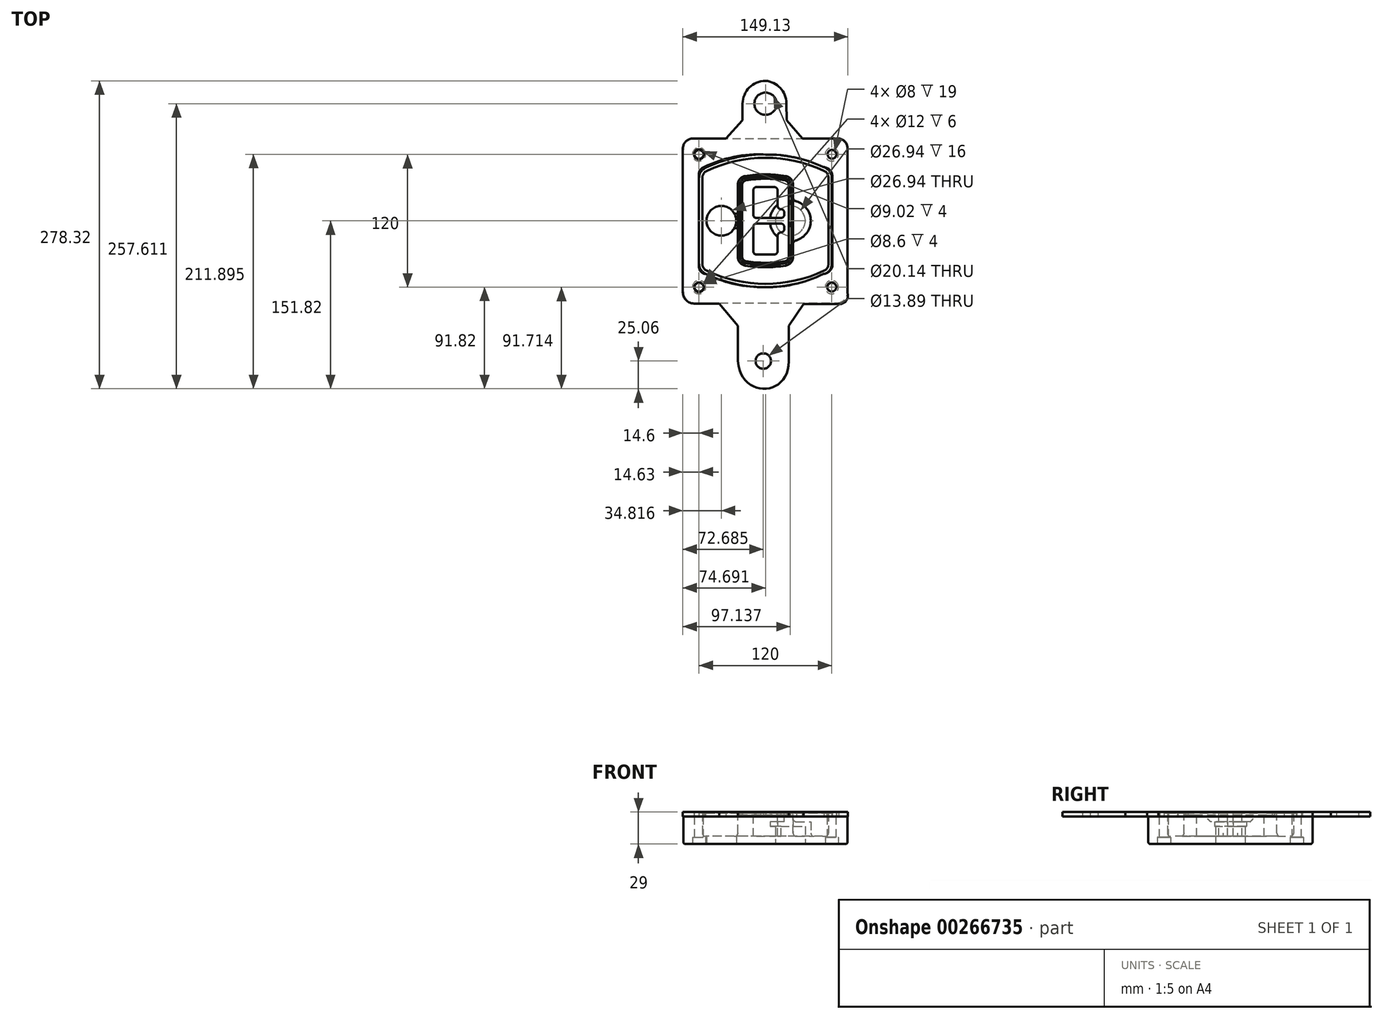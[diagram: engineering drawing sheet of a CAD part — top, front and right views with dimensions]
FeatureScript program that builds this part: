
annotation { "Feature Type Name" : "Feature", "Feature Type Description" : "" }
export const myFeature = defineFeature(function(context is Context, id is Id, definition is map)
    precondition{}
    {
        {
            var Q0;
            Q0=qCreatedBy(makeId("Top.planeOp"),FACE);
            var sketch = newSketch(context, id + "F0", { "sketchPlane" : qUnion([Q0])});
            skPoint(sketch, "E0.rect.middle", {"position": v(0, 0) * mm});
            skLineSegment(sketch, "E1.bottom", {"start": v(-64.25, -74.25) * mm, "end": v(64.25, -74.25) * mm});
            skLineSegment(sketch, "E1.top", {"start": v(-64.25, 74.25) * mm, "end": v(64.25, 74.25) * mm});
            skLineSegment(sketch, "E1.left", {"start": v(-74.25, -64.25) * mm, "end": v(-74.25, 64.25) * mm});
            skLineSegment(sketch, "E1.right", {"start": v(74.25, -64.25) * mm, "end": v(74.25, 64.25) * mm});
            skLineSegment(sketch, "E2", {"start": v(-74.25, 74.25) * mm, "end": v(74.25, -74.25) * mm, "construction": true});
            skLineSegment(sketch, "E3", {"start": v(74.25, 74.25) * mm, "end": v(-74.25, -74.25) * mm, "construction": true});
            skCircle(sketch, "E4", {"center": v(-60, 60) * mm, "radius": 4 * mm});
            skCircle(sketch, "E5", {"center": v(60, 60) * mm, "radius": 4 * mm});
            skCircle(sketch, "E6", {"center": v(60, -60) * mm, "radius": 4 * mm});
            skCircle(sketch, "E7", {"center": v(-60, -60) * mm, "radius": 4 * mm});
            skLineSegment(sketch, "E8", {"start": v(-60, 60) * mm, "end": v(60, 60) * mm, "construction": true});
            skLineSegment(sketch, "E9", {"start": v(60, 60) * mm, "end": v(60, -60) * mm, "construction": true});
            skLineSegment(sketch, "E10", {"start": v(60, -60) * mm, "end": v(-60, -60) * mm, "construction": true});
            skLineSegment(sketch, "E11", {"start": v(-60, -60) * mm, "end": v(-60, 60) * mm, "construction": true});
            skLineSegment(sketch, "E12", {"start": v(-60, 38.83) * mm, "end": v(-60, -38.83) * mm});
            skLineSegment(sketch, "E13", {"start": v(60, 38.83) * mm, "end": v(60, -38.83) * mm});
            skArc(sketch, "E14", {"start": v(54.26, 47.88) * mm, "mid": v(0, 60) * mm, "end": v(-54.26, 47.88) * mm});
            skArc(sketch, "E15", {"start": v(-54.26, -47.88) * mm, "mid": v(0, -60) * mm, "end": v(54.26, -47.88) * mm});
            skLineSegment(sketch, "E16", {"start": v(-60, 0) * mm, "end": v(60, 0) * mm, "construction": true});
            skPoint(sketch, "E17.visualSharp", {"position": v(-60, -45) * mm});
            skArc(sketch, "E17.filletArc", {"start": v(-60, -38.83) * mm, "mid": v(-58.44, -44.2) * mm, "end": v(-54.26, -47.88) * mm});
            skPoint(sketch, "E18.visualSharp", {"position": v(-60, 45) * mm});
            skArc(sketch, "E18.filletArc", {"start": v(-54.26, 47.88) * mm, "mid": v(-58.44, 44.2) * mm, "end": v(-60, 38.83) * mm});
            skPoint(sketch, "E19.visualSharp", {"position": v(60, 45) * mm});
            skArc(sketch, "E19.filletArc", {"start": v(60, 38.83) * mm, "mid": v(58.44, 44.2) * mm, "end": v(54.26, 47.88) * mm});
            skPoint(sketch, "E20.visualSharp", {"position": v(60, -45) * mm});
            skArc(sketch, "E20.filletArc", {"start": v(54.26, -47.88) * mm, "mid": v(58.44, -44.2) * mm, "end": v(60, -38.83) * mm});
            skPoint(sketch, "E21.visualSharp", {"position": v(-74.25, 74.25) * mm});
            skArc(sketch, "E21.filletArc", {"start": v(-64.25, 74.25) * mm, "mid": v(-71.32, 71.32) * mm, "end": v(-74.25, 64.25) * mm});
            skPoint(sketch, "E22.visualSharp", {"position": v(74.25, 74.25) * mm});
            skArc(sketch, "E22.filletArc", {"start": v(74.25, 64.25) * mm, "mid": v(71.32, 71.32) * mm, "end": v(64.25, 74.25) * mm});
            skPoint(sketch, "E23.visualSharp", {"position": v(74.25, -74.25) * mm});
            skArc(sketch, "E23.filletArc", {"start": v(64.25, -74.25) * mm, "mid": v(71.32, -71.32) * mm, "end": v(74.25, -64.25) * mm});
            skPoint(sketch, "E24.visualSharp", {"position": v(-74.25, -74.25) * mm});
            skArc(sketch, "E24.filletArc", {"start": v(-74.25, -64.25) * mm, "mid": v(-71.32, -71.32) * mm, "end": v(-64.25, -74.25) * mm});
            skArc(sketch, "E25.0", {"start": v(57, 38.83) * mm, "mid": v(55.9, 42.58) * mm, "end": v(52.98, 45.17) * mm});
            skLineSegment(sketch, "E25.1", {"start": v(57, 38.83) * mm, "end": v(57, -38.83) * mm});
            skArc(sketch, "E25.2", {"start": v(52.98, -45.17) * mm, "mid": v(55.9, -42.58) * mm, "end": v(57, -38.83) * mm});
            skArc(sketch, "E25.3", {"start": v(-52.98, -45.17) * mm, "mid": v(0, -57) * mm, "end": v(52.98, -45.17) * mm});
            skArc(sketch, "E25.4", {"start": v(-57, -38.83) * mm, "mid": v(-55.9, -42.58) * mm, "end": v(-52.98, -45.17) * mm});
            skArc(sketch, "E25.5", {"start": v(52.98, 45.17) * mm, "mid": v(0, 57) * mm, "end": v(-52.98, 45.17) * mm});
            skLineSegment(sketch, "E25.6", {"start": v(-57, 38.83) * mm, "end": v(-57, -38.83) * mm});
            skArc(sketch, "E25.7", {"start": v(-52.98, 45.17) * mm, "mid": v(-55.9, 42.58) * mm, "end": v(-57, 38.83) * mm});
            skArc(sketch, "E26.0", {"start": v(-55.96, 51.5) * mm, "mid": v(-61.82, 46.33) * mm, "end": v(-64, 38.83) * mm});
            skArc(sketch, "E26.1", {"start": v(55.96, 51.5) * mm, "mid": v(0, 64) * mm, "end": v(-55.96, 51.5) * mm});
            skArc(sketch, "E26.2", {"start": v(64, 38.83) * mm, "mid": v(61.82, 46.33) * mm, "end": v(55.96, 51.5) * mm});
            skLineSegment(sketch, "E26.3", {"start": v(64, 38.83) * mm, "end": v(64, -38.83) * mm});
            skArc(sketch, "E26.4", {"start": v(55.96, -51.5) * mm, "mid": v(61.82, -46.33) * mm, "end": v(64, -38.83) * mm});
            skLineSegment(sketch, "E26.5", {"start": v(-64, 38.83) * mm, "end": v(-64, -38.83) * mm});
            skArc(sketch, "E26.6", {"start": v(-55.96, -51.5) * mm, "mid": v(0, -64) * mm, "end": v(55.96, -51.5) * mm});
            skArc(sketch, "E26.7", {"start": v(-64, -38.83) * mm, "mid": v(-61.82, -46.33) * mm, "end": v(-55.96, -51.5) * mm});
            skSolve(sketch);
        }
        {
            var Q0;
            Q0=makeQuery(id+"F0.imprint","IMPRINT",FACE,{"disambiguationData":[TD([[makeQuery(id+"F0.imprint","IMPRINT",EDGE,{"derivedFrom":sQuery(id+"F0.wireOp",EDGE,"E1.bottom")}),1.0]])]});
            var Q1;
            Q1=makeQuery(id+"F0.imprint","IMPRINT",FACE,{"disambiguationData":[TD([[makeQuery(id+"F0.imprint","IMPRINT",EDGE,{"derivedFrom":sQuery(id+"F0.wireOp",EDGE,"E12")}),1.0]])]});
            var Q2;
            Q2=makeQuery(id+"F0.imprint","IMPRINT",FACE,{"disambiguationData":[TD([[makeQuery(id+"F0.imprint","IMPRINT",EDGE,{"derivedFrom":sQuery(id+"F0.wireOp",EDGE,"E25.0")}),1.0]])]});
            var Q3;
            Q3=makeQuery(id+"F0.imprint","IMPRINT",FACE,{"disambiguationData":[TD([[makeQuery(id+"F0.imprint","IMPRINT",EDGE,{"derivedFrom":sQuery(id+"F0.wireOp",EDGE,"E12")}),-1.0]])]});
            extrude(context, id + "F1", {"entities" : qUnion([Q0, Q1, Q2, Q3]), "oppositeDirection" : true, "depth" : 25 * mm});
        }
        {
            var Q0;
            Q0=makeQuery(id+"F0.imprint","IMPRINT",FACE,{"disambiguationData":[TD([[makeQuery(id+"F0.imprint","IMPRINT",EDGE,{"derivedFrom":sQuery(id+"F0.wireOp",EDGE,"E12")}),1.0]])]});
            extrude(context, id + "F2", {"entities" : qUnion([Q0]), "operationType" : NewBodyOperationType.ADD, "depth" : 3 * mm});
        }
        {
            var Q0;
            Q0=makeQuery(id+"F0.imprint","IMPRINT",FACE,{"disambiguationData":[TD([[makeQuery(id+"F0.imprint","IMPRINT",EDGE,{"derivedFrom":sQuery(id+"F0.wireOp",EDGE,"E25.0")}),1.0]])]});
            extrude(context, id + "F3", {"entities" : qUnion([Q0]), "operationType" : NewBodyOperationType.REMOVE, "oppositeDirection" : true, "depth" : 18 * mm});
        }
        {
            var Q0;
            Q0=makeQuery(id+"F2.opExtrude","CAP_FACE",FACE,{"disambiguationData":[OSD([sQuery(id+"F0.wireOp",EDGE,"E12"),sQuery(id+"F0.wireOp",EDGE,"E13"),sQuery(id+"F0.wireOp",EDGE,"E14"),sQuery(id+"F0.wireOp",EDGE,"E15"),sQuery(id+"F0.wireOp",EDGE,"E17.filletArc"),sQuery(id+"F0.wireOp",EDGE,"E18.filletArc"),sQuery(id+"F0.wireOp",EDGE,"E19.filletArc"),sQuery(id+"F0.wireOp",EDGE,"E20.filletArc"),sQuery(id+"F0.wireOp",EDGE,"E25.0"),sQuery(id+"F0.wireOp",EDGE,"E25.1"),sQuery(id+"F0.wireOp",EDGE,"E25.2"),sQuery(id+"F0.wireOp",EDGE,"E25.3"),sQuery(id+"F0.wireOp",EDGE,"E25.4"),sQuery(id+"F0.wireOp",EDGE,"E25.5"),sQuery(id+"F0.wireOp",EDGE,"E25.6"),sQuery(id+"F0.wireOp",EDGE,"E25.7")])],"isStart":false});
            var sketch = newSketch(context, id + "F4", { "sketchPlane" : qUnion([Q0])});
            skArc(sketch, "E27.0", {"start": v(-18.34, -40.45) * mm, "mid": v(0, -42) * mm, "end": v(18.34, -40.45) * mm});
            skArc(sketch, "E28.0", {"start": v(18.34, 40.45) * mm, "mid": v(0, 42) * mm, "end": v(-18.34, 40.45) * mm});
            skLineSegment(sketch, "E29", {"start": v(-25, 32.57) * mm, "end": v(-25, -32.57) * mm});
            skLineSegment(sketch, "E30", {"start": v(25, 32.57) * mm, "end": v(25, -32.57) * mm});
            skLineSegment(sketch, "E31", {"start": v(-25, 39.1) * mm, "end": v(25, 39.1) * mm, "construction": true});
            skLineSegment(sketch, "E32", {"start": v(-25, -39.1) * mm, "end": v(25, -39.1) * mm, "construction": true});
            skPoint(sketch, "E33.visualSharp", {"position": v(-25, 39.1) * mm});
            skArc(sketch, "E33.filletArc", {"start": v(-18.34, 40.45) * mm, "mid": v(-23.11, 37.73) * mm, "end": v(-25, 32.57) * mm});
            skPoint(sketch, "E34.visualSharp", {"position": v(25, 39.1) * mm});
            skArc(sketch, "E34.filletArc", {"start": v(25, 32.57) * mm, "mid": v(23.11, 37.73) * mm, "end": v(18.34, 40.45) * mm});
            skPoint(sketch, "E35.visualSharp", {"position": v(25, -39.1) * mm});
            skArc(sketch, "E35.filletArc", {"start": v(18.34, -40.45) * mm, "mid": v(23.11, -37.73) * mm, "end": v(25, -32.57) * mm});
            skPoint(sketch, "E36.visualSharp", {"position": v(-25, -39.1) * mm});
            skArc(sketch, "E36.filletArc", {"start": v(-25, -32.57) * mm, "mid": v(-23.11, -37.73) * mm, "end": v(-18.34, -40.45) * mm});
            skArc(sketch, "E37.0", {"start": v(52.98, 45.17) * mm, "mid": v(0, 57) * mm, "end": v(-52.98, 45.17) * mm});
            skArc(sketch, "E37.1", {"start": v(-52.98, 45.17) * mm, "mid": v(-55.9, 42.58) * mm, "end": v(-57, 38.83) * mm});
            skLineSegment(sketch, "E37.2", {"start": v(-57, 38.83) * mm, "end": v(-57, -38.83) * mm});
            skArc(sketch, "E37.3", {"start": v(-57, -38.83) * mm, "mid": v(-55.9, -42.58) * mm, "end": v(-52.98, -45.17) * mm});
            skArc(sketch, "E37.4", {"start": v(-52.98, -45.17) * mm, "mid": v(0, -57) * mm, "end": v(52.98, -45.17) * mm});
            skArc(sketch, "E37.5", {"start": v(52.98, -45.17) * mm, "mid": v(55.9, -42.58) * mm, "end": v(57, -38.83) * mm});
            skLineSegment(sketch, "E37.6", {"start": v(57, 38.83) * mm, "end": v(57, -38.83) * mm});
            skArc(sketch, "E37.7", {"start": v(57, 38.83) * mm, "mid": v(55.9, 42.58) * mm, "end": v(52.98, 45.17) * mm});
            skLineSegment(sketch, "E38.0", {"start": v(23, 32.57) * mm, "end": v(23, -32.57) * mm});
            skArc(sketch, "E38.1", {"start": v(18, -38.48) * mm, "mid": v(21.58, -36.44) * mm, "end": v(23, -32.57) * mm});
            skArc(sketch, "E38.2", {"start": v(-18, -38.48) * mm, "mid": v(0, -40) * mm, "end": v(18, -38.48) * mm});
            skArc(sketch, "E38.3", {"start": v(-23, -32.57) * mm, "mid": v(-21.58, -36.44) * mm, "end": v(-18, -38.48) * mm});
            skLineSegment(sketch, "E38.4", {"start": v(-23, 32.57) * mm, "end": v(-23, -32.57) * mm});
            skArc(sketch, "E38.5", {"start": v(23, 32.57) * mm, "mid": v(21.58, 36.44) * mm, "end": v(18, 38.48) * mm});
            skArc(sketch, "E38.6", {"start": v(-18, 38.48) * mm, "mid": v(-21.58, 36.44) * mm, "end": v(-23, 32.57) * mm});
            skArc(sketch, "E38.7", {"start": v(18, 38.48) * mm, "mid": v(0, 40) * mm, "end": v(-18, 38.48) * mm});
            skArc(sketch, "E39.0", {"start": v(21, 32.57) * mm, "mid": v(20.06, 35.15) * mm, "end": v(17.67, 36.5) * mm});
            skLineSegment(sketch, "E39.1", {"start": v(21, 32.57) * mm, "end": v(21, -32.57) * mm});
            skArc(sketch, "E39.2", {"start": v(17.67, -36.5) * mm, "mid": v(20.06, -35.15) * mm, "end": v(21, -32.57) * mm});
            skArc(sketch, "E39.3", {"start": v(-17.67, -36.5) * mm, "mid": v(0, -38) * mm, "end": v(17.67, -36.5) * mm});
            skArc(sketch, "E39.4", {"start": v(-21, -32.57) * mm, "mid": v(-20.06, -35.15) * mm, "end": v(-17.67, -36.5) * mm});
            skArc(sketch, "E39.5", {"start": v(17.67, 36.5) * mm, "mid": v(0, 38) * mm, "end": v(-17.67, 36.5) * mm});
            skLineSegment(sketch, "E39.6", {"start": v(-21, 32.57) * mm, "end": v(-21, -32.57) * mm});
            skArc(sketch, "E39.7", {"start": v(-17.67, 36.5) * mm, "mid": v(-20.06, 35.15) * mm, "end": v(-21, 32.57) * mm});
            skLineSegment(sketch, "E40", {"start": v(-25, 0) * mm, "end": v(25, 0) * mm, "construction": true});
            skLineSegment(sketch, "E41", {"start": v(-11, 5.5) * mm, "end": v(-11, 27.5) * mm});
            skLineSegment(sketch, "E42", {"start": v(-8, 30.5) * mm, "end": v(8, 30.5) * mm});
            skLineSegment(sketch, "E43", {"start": v(11, 27.5) * mm, "end": v(11, 13.5) * mm});
            skLineSegment(sketch, "E44", {"start": v(14, 10.5) * mm, "end": v(14, 10.5) * mm});
            skLineSegment(sketch, "E45", {"start": v(17, 7.5) * mm, "end": v(17, 5.5) * mm});
            skLineSegment(sketch, "E46", {"start": v(14, 2.5) * mm, "end": v(-8, 2.5) * mm});
            skPoint(sketch, "E47.visualSharp", {"position": v(-11, 30.5) * mm});
            skArc(sketch, "E47.filletArc", {"start": v(-8, 30.5) * mm, "mid": v(-10.12, 29.62) * mm, "end": v(-11, 27.5) * mm});
            skPoint(sketch, "E48.visualSharp", {"position": v(11, 30.5) * mm});
            skArc(sketch, "E48.filletArc", {"start": v(11, 27.5) * mm, "mid": v(10.12, 29.62) * mm, "end": v(8, 30.5) * mm});
            skPoint(sketch, "E49.visualSharp", {"position": v(11, 10.5) * mm});
            skArc(sketch, "E49.filletArc", {"start": v(11, 13.5) * mm, "mid": v(11.88, 11.38) * mm, "end": v(14, 10.5) * mm});
            skPoint(sketch, "E50.visualSharp", {"position": v(17, 10.5) * mm});
            skArc(sketch, "E50.filletArc", {"start": v(17, 7.5) * mm, "mid": v(16.12, 9.62) * mm, "end": v(14, 10.5) * mm});
            skPoint(sketch, "E51.visualSharp", {"position": v(17, 2.5) * mm});
            skArc(sketch, "E51.filletArc", {"start": v(14, 2.5) * mm, "mid": v(16.12, 3.38) * mm, "end": v(17, 5.5) * mm});
            skPoint(sketch, "E52.visualSharp", {"position": v(-11, 2.5) * mm});
            skArc(sketch, "E52.filletArc", {"start": v(-11, 5.5) * mm, "mid": v(-10.12, 3.38) * mm, "end": v(-8, 2.5) * mm});
            skLineSegment(sketch, "E53.0.MirrorCS", {"start": v(14, -2.5) * mm, "end": v(-8, -2.5) * mm});
            skArc(sketch, "E54.0.MirrorCS", {"start": v(-11, -5.5) * mm, "mid": v(-10.12, -3.38) * mm, "end": v(-8, -2.5) * mm});
            skLineSegment(sketch, "E55.0.MirrorCS", {"start": v(-11, -5.5) * mm, "end": v(-11, -27.5) * mm});
            skArc(sketch, "E56.0.MirrorCS", {"start": v(-8, -30.5) * mm, "mid": v(-10.12, -29.62) * mm, "end": v(-11, -27.5) * mm});
            skLineSegment(sketch, "E57.0.MirrorCS", {"start": v(-8, -30.5) * mm, "end": v(8, -30.5) * mm});
            skArc(sketch, "E58.0.MirrorCS", {"start": v(11, -27.5) * mm, "mid": v(10.12, -29.62) * mm, "end": v(8, -30.5) * mm});
            skLineSegment(sketch, "E59.0.MirrorCS", {"start": v(11, -27.5) * mm, "end": v(11, -13.5) * mm});
            skArc(sketch, "E60.0.MirrorCS", {"start": v(11, -13.5) * mm, "mid": v(11.88, -11.38) * mm, "end": v(14, -10.5) * mm});
            skArc(sketch, "E61.0.MirrorCS", {"start": v(17, -7.5) * mm, "mid": v(16.12, -9.62) * mm, "end": v(14, -10.5) * mm});
            skLineSegment(sketch, "E62.0.MirrorCS", {"start": v(17, -7.5) * mm, "end": v(17, -5.5) * mm});
            skArc(sketch, "E63.0.MirrorCS", {"start": v(14, -2.5) * mm, "mid": v(16.12, -3.38) * mm, "end": v(17, -5.5) * mm});
            skSolve(sketch);
        }
        {
            var Q0;
            Q0=makeQuery(id+"F4.imprint","IMPRINT",FACE,{"disambiguationData":[TD([[makeQuery(id+"F4.imprint","IMPRINT",EDGE,{"derivedFrom":sQuery(id+"F4.wireOp",EDGE,"E27.0")}),1.0]])]});
            var Q1;
            Q1=makeQuery(id+"F4.imprint","IMPRINT",FACE,{"disambiguationData":[TD([[makeQuery(id+"F4.imprint","IMPRINT",EDGE,{"derivedFrom":sQuery(id+"F4.wireOp",EDGE,"E38.0")}),-1.0]])]});
            var Q2;
            Q2=makeQuery(id+"F4.imprint","IMPRINT",FACE,{"disambiguationData":[TD([[makeQuery(id+"F4.imprint","IMPRINT",EDGE,{"derivedFrom":sQuery(id+"F4.wireOp",EDGE,"E39.0")}),1.0]])]});
            extrude(context, id + "F5", {"entities" : qUnion([Q0, Q1, Q2]), "operationType" : NewBodyOperationType.ADD, "endBound" : BoundingType.UP_TO_NEXT, "oppositeDirection" : true, "depth" : 25 * mm});
        }
        {
            var Q0;
            Q0=makeQuery(id+"F4.imprint","IMPRINT",FACE,{"disambiguationData":[TD([[makeQuery(id+"F4.imprint","IMPRINT",EDGE,{"derivedFrom":sQuery(id+"F4.wireOp",EDGE,"E38.0")}),-1.0]])]});
            extrude(context, id + "F6", {"entities" : qUnion([Q0]), "operationType" : NewBodyOperationType.REMOVE, "oppositeDirection" : true, "depth" : 2 * mm});
        }
        {
            var Q0;
            Q0=makeQuery(id+"F1.opExtrude","CAP_FACE",FACE,{"disambiguationData":[OSD([sQuery(id+"F0.wireOp",EDGE,"E1.bottom"),sQuery(id+"F0.wireOp",EDGE,"E1.top"),sQuery(id+"F0.wireOp",EDGE,"E1.left"),sQuery(id+"F0.wireOp",EDGE,"E1.right"),sQuery(id+"F0.wireOp",EDGE,"E4"),sQuery(id+"F0.wireOp",EDGE,"E5"),sQuery(id+"F0.wireOp",EDGE,"E6"),sQuery(id+"F0.wireOp",EDGE,"E7"),sQuery(id+"F0.wireOp",EDGE,"E21.filletArc"),sQuery(id+"F0.wireOp",EDGE,"E22.filletArc"),sQuery(id+"F0.wireOp",EDGE,"E23.filletArc"),sQuery(id+"F0.wireOp",EDGE,"E24.filletArc")])],"isStart":false});
            var sketch = newSketch(context, id + "F7", { "sketchPlane" : qUnion([Q0])});
            skCircle(sketch, "E64", {"center": v(22.5, 0) * mm, "radius": 13.47 * mm});
            skCircle(sketch, "E65", {"center": v(-39.81, 0) * mm, "radius": 13.47 * mm});
            skLineSegment(sketch, "E66", {"start": v(74.25, 0) * mm, "end": v(-74.25, 0) * mm});
            skCircle(sketch, "E67", {"center": v(22.5, 0) * mm, "radius": 18.47 * mm});
            skCircle(sketch, "E68", {"center": v(60, -60) * mm, "radius": 6 * mm});
            skCircle(sketch, "E69", {"center": v(-60, -60) * mm, "radius": 6 * mm});
            skCircle(sketch, "E70", {"center": v(-60, 60) * mm, "radius": 6 * mm});
            skCircle(sketch, "E71", {"center": v(60, 60) * mm, "radius": 6 * mm});
            skSolve(sketch);
        }
        {
            var Q0;
            {var subQ1=sQuery(id+"F7.wireOp",EDGE,"E66");var subQ4=sQuery(id+"F7.wireOp",EDGE,"E64");var subQ6=makeQuery(id+"F7.imprint","INTERSECT",VERTEX,{"disambiguationData":[OD(0.0)],"derivedFrom":[subQ4,subQ1]});Q0=makeQuery(id+"F7.imprint","IMPRINT",FACE,{"disambiguationData":[TD([[makeQuery(id+"F7.imprint","IMPRINT",EDGE,{"disambiguationData":[TD([[subQ6,-1.0]])],"derivedFrom":subQ4}),-1.0]])]});}
            var Q1;
            {var subQ0=sQuery(id+"F7.wireOp",EDGE,"E66");var subQ1=sQuery(id+"F7.wireOp",EDGE,"E64");var subQ3=makeQuery(id+"F7.imprint","INTERSECT",VERTEX,{"disambiguationData":[OD(0.0)],"derivedFrom":[subQ1,subQ0]});Q1=makeQuery(id+"F7.imprint","IMPRINT",FACE,{"disambiguationData":[TD([[makeQuery(id+"F7.imprint","IMPRINT",EDGE,{"disambiguationData":[TD([[subQ3,-1.0]])],"derivedFrom":subQ1}),1.0]])]});}
            var Q2;
            {var subQ0=sQuery(id+"F7.wireOp",EDGE,"E66");var subQ1=sQuery(id+"F7.wireOp",EDGE,"E64");var subQ3=makeQuery(id+"F7.imprint","INTERSECT",VERTEX,{"disambiguationData":[OD(0.0)],"derivedFrom":[subQ1,subQ0]});Q2=makeQuery(id+"F7.imprint","IMPRINT",FACE,{"disambiguationData":[TD([[makeQuery(id+"F7.imprint","IMPRINT",EDGE,{"disambiguationData":[TD([[subQ3,1.0]])],"derivedFrom":subQ1}),1.0]])]});}
            var Q3;
            {var subQ1=sQuery(id+"F7.wireOp",EDGE,"E66");var subQ4=sQuery(id+"F7.wireOp",EDGE,"E64");var subQ6=makeQuery(id+"F7.imprint","INTERSECT",VERTEX,{"disambiguationData":[OD(0.0)],"derivedFrom":[subQ4,subQ1]});Q3=makeQuery(id+"F7.imprint","IMPRINT",FACE,{"disambiguationData":[TD([[makeQuery(id+"F7.imprint","IMPRINT",EDGE,{"disambiguationData":[TD([[subQ6,1.0]])],"derivedFrom":subQ4}),-1.0]])]});}
            extrude(context, id + "F8", {"entities" : qUnion([Q0, Q1, Q2, Q3]), "operationType" : NewBodyOperationType.ADD, "oppositeDirection" : true, "depth" : 20 * mm});
        }
        {
            var Q0;
            {var subQ0=sQuery(id+"F7.wireOp",EDGE,"E66");var subQ1=sQuery(id+"F7.wireOp",EDGE,"E64");var subQ3=makeQuery(id+"F7.imprint","INTERSECT",VERTEX,{"disambiguationData":[OD(0.0)],"derivedFrom":[subQ1,subQ0]});Q0=makeQuery(id+"F7.imprint","IMPRINT",FACE,{"disambiguationData":[TD([[makeQuery(id+"F7.imprint","IMPRINT",EDGE,{"disambiguationData":[TD([[subQ3,-1.0]])],"derivedFrom":subQ1}),1.0]])]});}
            var Q1;
            {var subQ0=sQuery(id+"F7.wireOp",EDGE,"E66");var subQ1=sQuery(id+"F7.wireOp",EDGE,"E64");var subQ3=makeQuery(id+"F7.imprint","INTERSECT",VERTEX,{"disambiguationData":[OD(0.0)],"derivedFrom":[subQ1,subQ0]});Q1=makeQuery(id+"F7.imprint","IMPRINT",FACE,{"disambiguationData":[TD([[makeQuery(id+"F7.imprint","IMPRINT",EDGE,{"disambiguationData":[TD([[subQ3,1.0]])],"derivedFrom":subQ1}),1.0]])]});}
            extrude(context, id + "F9", {"entities" : qUnion([Q0, Q1]), "operationType" : NewBodyOperationType.REMOVE, "oppositeDirection" : true, "depth" : 16 * mm});
        }
        {
            var Q0;
            {var subQ0=sQuery(id+"F7.wireOp",EDGE,"E66");var subQ1=sQuery(id+"F7.wireOp",EDGE,"E65");var subQ3=makeQuery(id+"F7.imprint","INTERSECT",VERTEX,{"disambiguationData":[OD(0.0)],"derivedFrom":[subQ1,subQ0]});Q0=makeQuery(id+"F7.imprint","IMPRINT",FACE,{"disambiguationData":[TD([[makeQuery(id+"F7.imprint","IMPRINT",EDGE,{"disambiguationData":[TD([[subQ3,-1.0]])],"derivedFrom":subQ1}),1.0]])]});}
            var Q1;
            {var subQ0=sQuery(id+"F7.wireOp",EDGE,"E66");var subQ1=sQuery(id+"F7.wireOp",EDGE,"E65");var subQ3=makeQuery(id+"F7.imprint","INTERSECT",VERTEX,{"disambiguationData":[OD(0.0)],"derivedFrom":[subQ1,subQ0]});Q1=makeQuery(id+"F7.imprint","IMPRINT",FACE,{"disambiguationData":[TD([[makeQuery(id+"F7.imprint","IMPRINT",EDGE,{"disambiguationData":[TD([[subQ3,1.0]])],"derivedFrom":subQ1}),1.0]])]});}
            extrude(context, id + "F10", {"entities" : qUnion([Q0, Q1]), "operationType" : NewBodyOperationType.REMOVE, "oppositeDirection" : true, "depth" : 25 * mm});
        }
        {
            var Q0;
            Q0=makeQuery(id+"F7.imprint","IMPRINT",FACE,{"disambiguationData":[TD([[makeQuery(id+"F7.imprint","IMPRINT",EDGE,{"derivedFrom":sQuery(id+"F7.wireOp",EDGE,"E68")}),1.0]])]});
            var Q1;
            Q1=makeQuery(id+"F7.imprint","IMPRINT",FACE,{"disambiguationData":[TD([[makeQuery(id+"F7.imprint","IMPRINT",EDGE,{"derivedFrom":makeQuery(id+"F1.opExtrude","CAP_EDGE",EDGE,{"disambiguationData":[OSD([sQuery(id+"F0.wireOp",EDGE,"E5")])],"isStart":false})}),-1.0]])]});
            var Q2;
            Q2=makeQuery(id+"F7.imprint","IMPRINT",FACE,{"disambiguationData":[TD([[makeQuery(id+"F7.imprint","IMPRINT",EDGE,{"derivedFrom":sQuery(id+"F7.wireOp",EDGE,"E69")}),1.0]])]});
            var Q3;
            Q3=makeQuery(id+"F7.imprint","IMPRINT",FACE,{"disambiguationData":[TD([[makeQuery(id+"F7.imprint","IMPRINT",EDGE,{"derivedFrom":makeQuery(id+"F1.opExtrude","CAP_EDGE",EDGE,{"disambiguationData":[OSD([sQuery(id+"F0.wireOp",EDGE,"E4")])],"isStart":false})}),-1.0]])]});
            var Q4;
            Q4=makeQuery(id+"F7.imprint","IMPRINT",FACE,{"disambiguationData":[TD([[makeQuery(id+"F7.imprint","IMPRINT",EDGE,{"derivedFrom":sQuery(id+"F7.wireOp",EDGE,"E70")}),1.0]])]});
            var Q5;
            Q5=makeQuery(id+"F7.imprint","IMPRINT",FACE,{"disambiguationData":[TD([[makeQuery(id+"F7.imprint","IMPRINT",EDGE,{"derivedFrom":makeQuery(id+"F1.opExtrude","CAP_EDGE",EDGE,{"disambiguationData":[OSD([sQuery(id+"F0.wireOp",EDGE,"E7")])],"isStart":false})}),-1.0]])]});
            var Q6;
            Q6=makeQuery(id+"F7.imprint","IMPRINT",FACE,{"disambiguationData":[TD([[makeQuery(id+"F7.imprint","IMPRINT",EDGE,{"derivedFrom":sQuery(id+"F7.wireOp",EDGE,"E71")}),1.0]])]});
            var Q7;
            Q7=makeQuery(id+"F7.imprint","IMPRINT",FACE,{"disambiguationData":[TD([[makeQuery(id+"F7.imprint","IMPRINT",EDGE,{"derivedFrom":makeQuery(id+"F1.opExtrude","CAP_EDGE",EDGE,{"disambiguationData":[OSD([sQuery(id+"F0.wireOp",EDGE,"E6")])],"isStart":false})}),-1.0]])]});
            extrude(context, id + "F11", {"entities" : qUnion([Q0, Q1, Q2, Q3, Q4, Q5, Q6, Q7]), "operationType" : NewBodyOperationType.REMOVE, "oppositeDirection" : true, "depth" : 6 * mm});
        }
        {
            var Q0;
            Q0=makeQuery(id+"F9.boolean.opBoolean","COPY",FACE,{"derivedFrom":makeQuery(id+"F9.opExtrude","CAP_FACE",FACE,{"disambiguationData":[OSD([sQuery(id+"F7.wireOp",EDGE,"E64")])],"isStart":false})});
            var sketch = newSketch(context, id + "F12", { "sketchPlane" : qUnion([Q0])});
            skArc(sketch, "E72.0", {"start": v(11, 14.45) * mm, "mid": v(6.45, 9.13) * mm, "end": v(4.2, 2.5) * mm});
            skArc(sketch, "E72.1", {"start": v(4.2, -2.5) * mm, "mid": v(6.45, -9.13) * mm, "end": v(11, -14.45) * mm});
            skLineSegment(sketch, "E73", {"start": v(4.2, -2.5) * mm, "end": v(14, -2.5) * mm});
            skLineSegment(sketch, "E74.0", {"start": v(14, 2.5) * mm, "end": v(4.2, 2.5) * mm});
            skArc(sketch, "E74.1", {"start": v(14, 2.5) * mm, "mid": v(16.12, 3.38) * mm, "end": v(17, 5.5) * mm});
            skLineSegment(sketch, "E74.2", {"start": v(17, 7.5) * mm, "end": v(17, 5.5) * mm});
            skArc(sketch, "E74.3", {"start": v(17, 7.5) * mm, "mid": v(16.12, 9.62) * mm, "end": v(14, 10.5) * mm});
            skArc(sketch, "E74.4", {"start": v(11, 13.5) * mm, "mid": v(11.88, 11.38) * mm, "end": v(14, 10.5) * mm});
            skLineSegment(sketch, "E74.5", {"start": v(11, 14.45) * mm, "end": v(11, 13.5) * mm});
            skLineSegment(sketch, "E74.7", {"start": v(14, -2.5) * mm, "end": v(4.2, -2.5) * mm});
            skArc(sketch, "E74.8", {"start": v(14, -2.5) * mm, "mid": v(16.12, -3.38) * mm, "end": v(17, -5.5) * mm});
            skLineSegment(sketch, "E74.9", {"start": v(17, -7.5) * mm, "end": v(17, -5.5) * mm});
            skArc(sketch, "E74.10", {"start": v(17, -7.5) * mm, "mid": v(16.12, -9.62) * mm, "end": v(14, -10.5) * mm});
            skArc(sketch, "E74.11", {"start": v(11, -13.5) * mm, "mid": v(11.88, -11.38) * mm, "end": v(14, -10.5) * mm});
            skLineSegment(sketch, "E74.12", {"start": v(11, -14.45) * mm, "end": v(11, -13.5) * mm});
            skPoint(sketch, "E75.orphan", {"position": v(11, -27.5) * mm});
            skPoint(sketch, "E76.orphan", {"position": v(-8, -2.5) * mm});
            skPoint(sketch, "E77.orphan", {"position": v(-8, 2.5) * mm});
            skPoint(sketch, "E78.orphan", {"position": v(11, 27.5) * mm});
            skSolve(sketch);
        }
        {
            var Q0;
            {var subQ7=sQuery(id+"F12.wireOp",EDGE,"E72.0");var subQ14=sQuery(id+"F12.wireOp",EDGE,"E72.1");var subQ16=sQuery(id+"F12.wireOp",EDGE,"E74.1");var subQ18=sQuery(id+"F12.wireOp",EDGE,"E74.8");Q0=qUnion([makeQuery(id+"F12.imprint","IMPRINT",FACE,{"disambiguationData":[TD([[makeQuery(id+"F12.imprint","IMPRINT",EDGE,{"derivedFrom":subQ7}),1.0]])]}),makeQuery(id+"F12.imprint","IMPRINT",FACE,{"disambiguationData":[TD([[makeQuery(id+"F12.imprint","IMPRINT",EDGE,{"derivedFrom":subQ14}),1.0]])]}),makeQuery(id+"F12.imprint","IMPRINT",FACE,{"disambiguationData":[TD([[makeQuery(id+"F12.imprint","IMPRINT",EDGE,{"derivedFrom":subQ16}),1.0]])]}),makeQuery(id+"F12.imprint","IMPRINT",FACE,{"disambiguationData":[TD([[makeQuery(id+"F12.imprint","IMPRINT",EDGE,{"derivedFrom":subQ18}),-1.0]])]})]);}
            var Q1;
            Q1=makeQuery(id+"F5.boolean.opBoolean","SPLIT",FACE,{"disambiguationData":[TD([makeQuery(id+"F5.opExtrude","SWEPT_FACE",FACE,{"disambiguationData":[OSD([sQuery(id+"F4.wireOp",EDGE,"E41")])]})])],"derivedFrom":makeQuery(id+"F3.boolean.opBoolean","COPY",FACE,{"derivedFrom":makeQuery(id+"F3.opExtrude","CAP_FACE",FACE,{"disambiguationData":[OSD([sQuery(id+"F0.wireOp",EDGE,"E25.0"),sQuery(id+"F0.wireOp",EDGE,"E25.1"),sQuery(id+"F0.wireOp",EDGE,"E25.2"),sQuery(id+"F0.wireOp",EDGE,"E25.3"),sQuery(id+"F0.wireOp",EDGE,"E25.4"),sQuery(id+"F0.wireOp",EDGE,"E25.5"),sQuery(id+"F0.wireOp",EDGE,"E25.6"),sQuery(id+"F0.wireOp",EDGE,"E25.7")])],"isStart":false})})});
            extrude(context, id + "F13", {"entities" : qUnion([Q0]), "operationType" : NewBodyOperationType.REMOVE, "endBound" : BoundingType.UP_TO_SURFACE, "endBoundEntityFace" : qUnion([Q1]), "depth" : 25 * mm});
        }
        {
            var Q0;
            Q0=makeQuery(id+"F3.boolean.opBoolean","COPY",EDGE,{"derivedFrom":makeQuery(id+"F3.opExtrude","CAP_EDGE",EDGE,{"disambiguationData":[OSD([sQuery(id+"F0.wireOp",EDGE,"E25.6")])],"isStart":false})});
            var Q1;
            Q1=makeQuery(id+"F8.boolean.opBoolean","INTERSECT",EDGE,{"derivedFrom":[makeQuery(id+"F5.opExtrude","SWEPT_FACE",FACE,{"disambiguationData":[OSD([sQuery(id+"F4.wireOp",EDGE,"E30")])]}),makeQuery(id+"F8.opExtrude","CAP_FACE",FACE,{"disambiguationData":[OSD([sQuery(id+"F7.wireOp",EDGE,"E67")])],"isStart":false})]});
            var Q2;
            Q2=makeQuery(id+"F8.boolean.opBoolean","INTERSECT",EDGE,{"disambiguationData":[OD(1.0)],"derivedFrom":[makeQuery(id+"F5.opExtrude","SWEPT_FACE",FACE,{"disambiguationData":[OSD([sQuery(id+"F4.wireOp",EDGE,"E30")])]}),makeQuery(id+"F8.opExtrude","SWEPT_FACE",FACE,{"disambiguationData":[OSD([sQuery(id+"F7.wireOp",EDGE,"E67")])]})]});
            var Q3;
            {var subQ0=sQuery(id+"F4.wireOp",EDGE,"E30");Q3=makeQuery(id+"F8.boolean.opBoolean","SPLIT",EDGE,{"disambiguationData":[TD([makeQuery(id+"F5.opExtrude","SWEPT_FACE",FACE,{"disambiguationData":[OSD([sQuery(id+"F4.wireOp",EDGE,"E35.filletArc")])]})])],"derivedFrom":makeQuery(id+"F5.opExtrude","CAP_EDGE",EDGE,{"disambiguationData":[OSD([subQ0])],"isStart":false})});}
            var Q4;
            {var subQ0=sQuery(id+"F0.wireOp",EDGE,"E25.7");var subQ1=sQuery(id+"F0.wireOp",EDGE,"E25.1");var subQ2=sQuery(id+"F0.wireOp",EDGE,"E25.6");var subQ3=sQuery(id+"F0.wireOp",EDGE,"E25.5");var subQ4=sQuery(id+"F0.wireOp",EDGE,"E25.4");var subQ5=sQuery(id+"F0.wireOp",EDGE,"E25.0");var subQ6=sQuery(id+"F0.wireOp",EDGE,"E25.2");var subQ7=sQuery(id+"F0.wireOp",EDGE,"E25.3");Q4=makeQuery(id+"F8.boolean.opBoolean","INTERSECT",EDGE,{"derivedFrom":[makeQuery(id+"F5.boolean.opBoolean","SPLIT",FACE,{"disambiguationData":[TD([makeQuery(id+"F2.opExtrude","SWEPT_FACE",FACE,{"disambiguationData":[OSD([subQ5])]})])],"derivedFrom":makeQuery(id+"F3.boolean.opBoolean","COPY",FACE,{"derivedFrom":makeQuery(id+"F3.opExtrude","CAP_FACE",FACE,{"disambiguationData":[OSD([subQ5,subQ1,subQ6,subQ7,subQ4,subQ3,subQ2,subQ0])],"isStart":false})})}),makeQuery(id+"F8.opExtrude","SWEPT_FACE",FACE,{"disambiguationData":[OSD([sQuery(id+"F7.wireOp",EDGE,"E67")])]})]});}
            var Q5;
            Q5=makeQuery(id+"F8.boolean.opBoolean","INTERSECT",EDGE,{"disambiguationData":[OD(0.0)],"derivedFrom":[makeQuery(id+"F5.opExtrude","SWEPT_FACE",FACE,{"disambiguationData":[OSD([sQuery(id+"F4.wireOp",EDGE,"E30")])]}),makeQuery(id+"F8.opExtrude","SWEPT_FACE",FACE,{"disambiguationData":[OSD([sQuery(id+"F7.wireOp",EDGE,"E67")])]})]});
            fillet(context, id + "F14", {"entities" : qUnion([Q0, Q1, Q2, Q3, Q4, Q5]), "radius" : 3 * mm, "tangentPropagation" : true, "allowEdgeOverflow" : false});
        }
        {
            var Q0;
            Q0=makeQuery(id+"F1.opExtrude","CAP_EDGE",EDGE,{"disambiguationData":[OSD([sQuery(id+"F0.wireOp",EDGE,"E1.bottom")])],"isStart":false});
            fillet(context, id + "F15", {"entities" : qUnion([Q0]), "radius" : 2 * mm, "tangentPropagation" : true, "allowEdgeOverflow" : false});
        }
        {
            var Q0;
            Q0=qCreatedBy(makeId("Top.planeOp"),FACE);
            var sketch = newSketch(context, id + "F16", { "sketchPlane" : qUnion([Q0])});
            skCircle(sketch, "E79", {"center": v(-60.03, 60.07) * mm, "radius": 4.5 * mm});
            skCircle(sketch, "E80", {"center": v(60.15, 60.07) * mm, "radius": 3.98 * mm});
            skCircle(sketch, "E81", {"center": v(-60.03, -60.1) * mm, "radius": 4.3 * mm});
            skCircle(sketch, "E82", {"center": v(59.91, -59.87) * mm, "radius": 4.06 * mm});
            skPoint(sketch, "E83.visualSharp", {"position": v(-75.56, 75.13) * mm});
            skLineSegment(sketch, "E84", {"start": v(-74.63, 65.22) * mm, "end": v(-74.63, -64.73) * mm});
            skArc(sketch, "E85", {"start": v(-74.63, -64.73) * mm, "mid": v(-71.72, -71.8) * mm, "end": v(-64.66, -74.75) * mm});
            skLineSegment(sketch, "E86", {"start": v(-64.66, -74.75) * mm, "end": v(66.7, -75.36) * mm});
            skArc(sketch, "E87", {"start": v(66.7, -75.36) * mm, "mid": v(73, -72.18) * mm, "end": v(74.12, -65.2) * mm});
            skLineSegment(sketch, "E88", {"start": v(74.12, -65.2) * mm, "end": v(74.12, 65.89) * mm});
            skArc(sketch, "E89", {"start": v(74.12, 65.89) * mm, "mid": v(71.84, 71.68) * mm, "end": v(66.23, 74.36) * mm});
            skLineSegment(sketch, "E90", {"start": v(66.23, 74.36) * mm, "end": v(-65.62, 74.36) * mm});
            skArc(sketch, "E91", {"start": v(-65.62, 74.36) * mm, "mid": v(-72.04, 71.68) * mm, "end": v(-74.63, 65.22) * mm});
            skLineSegment(sketch, "E92", {"start": v(-41.84, -74.85) * mm, "end": v(-25, -95) * mm});
            skLineSegment(sketch, "E93", {"start": v(-25, -95) * mm, "end": v(-25, -126.76) * mm});
            skLineSegment(sketch, "E94", {"start": v(-25, -126.76) * mm, "end": v(21.12, -126.97) * mm});
            skLineSegment(sketch, "E95", {"start": v(21.12, -126.97) * mm, "end": v(21.12, -95) * mm});
            skLineSegment(sketch, "E96", {"start": v(21.12, -95) * mm, "end": v(34.51, -75.2) * mm});
            skLineSegment(sketch, "E97", {"start": v(34.51, -75.2) * mm, "end": v(-41.84, -74.85) * mm});
            skLineSegment(sketch, "E98", {"start": v(-35.6, 74.36) * mm, "end": v(-20.65, 90.84) * mm});
            skLineSegment(sketch, "E99", {"start": v(-20.65, 90.84) * mm, "end": v(-20.65, 105.8) * mm});
            skLineSegment(sketch, "E100", {"start": v(-20.65, 105.8) * mm, "end": v(18.9, 106.38) * mm});
            skLineSegment(sketch, "E101", {"start": v(18.9, 106.38) * mm, "end": v(19.14, 90.84) * mm});
            skLineSegment(sketch, "E102", {"start": v(19.14, 90.84) * mm, "end": v(33.47, 74.36) * mm});
            skLineSegment(sketch, "E103", {"start": v(33.47, 74.36) * mm, "end": v(-35.6, 74.36) * mm});
            skArc(sketch, "E104", {"start": v(0, 126.5) * mm, "mid": v(-14.6, 120.41) * mm, "end": v(-20.65, 105.8) * mm});
            skArc(sketch, "E105", {"start": v(18.9, 106.38) * mm, "mid": v(13.35, 120.1) * mm, "end": v(0, 126.5) * mm});
            skLineSegment(sketch, "E106", {"start": v(-60.06, 39.92) * mm, "end": v(-60.06, -41.58) * mm});
            skArc(sketch, "E107", {"start": v(-60.06, -41.58) * mm, "mid": v(-58.4, -45.9) * mm, "end": v(-54.28, -48) * mm});
            skArc(sketch, "E108", {"start": v(-54.28, -48) * mm, "mid": v(-29.9, -56.75) * mm, "end": v(-4.19, -60) * mm});
            skArc(sketch, "E109", {"start": v(-4.19, -60) * mm, "mid": v(24.93, -57.58) * mm, "end": v(52.54, -48) * mm});
            skArc(sketch, "E110", {"start": v(52.54, -48) * mm, "mid": v(57.46, -45.97) * mm, "end": v(60.46, -41.58) * mm});
            skLineSegment(sketch, "E111", {"start": v(60.46, -41.58) * mm, "end": v(60.46, 40.2) * mm});
            skArc(sketch, "E112", {"start": v(60.46, 40.2) * mm, "mid": v(58.1, 46.02) * mm, "end": v(52.33, 48.54) * mm});
            skArc(sketch, "E113", {"start": v(52.33, 48.54) * mm, "mid": v(26.8, 57.17) * mm, "end": v(0, 59.88) * mm});
            skArc(sketch, "E114", {"start": v(0, 59.88) * mm, "mid": v(-28.4, 57.78) * mm, "end": v(-55.35, 48.54) * mm});
            skArc(sketch, "E115", {"start": v(-55.35, 48.54) * mm, "mid": v(-59.42, 45.17) * mm, "end": v(-60.06, 39.92) * mm});
            skCircle(sketch, "E116", {"center": v(-1.94, -126.76) * mm, "radius": 6.95 * mm});
            skPoint(sketch, "E116.centerSnap0", {"position": v(-1.94, -126.87) * mm});
            skCircle(sketch, "E117", {"center": v(0.06, 105.8) * mm, "radius": 10.07 * mm});
            skFitSpline(sketch, "E118", {"points": [v(-25, -126.76) * mm, v(0, -151.8) * mm, v(21.12, -126.97) * mm], "startDerivative": vector(7.6, -102.13) * mm, "endDerivative": vector(-0.87, 95.76) * mm});
            skSolve(sketch);
        }
        {
            var Q0;
            Q0 = qSketchRegion(id + "F16", true);
            extrude(context, id + "F17", {"entities" : qUnion([Q0]), "operationType" : NewBodyOperationType.ADD, "depth" : 4 * mm});
        }
    });
